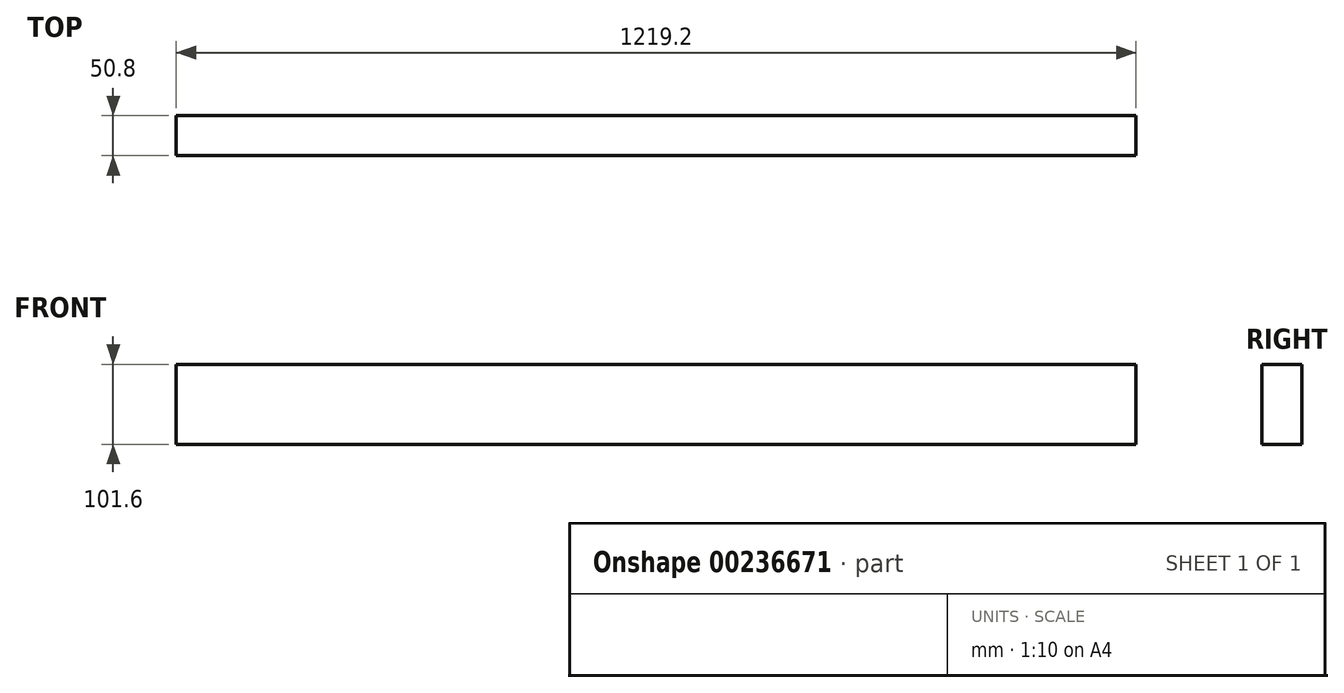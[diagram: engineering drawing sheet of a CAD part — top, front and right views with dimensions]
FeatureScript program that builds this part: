
annotation { "Feature Type Name" : "Feature", "Feature Type Description" : "" }
export const myFeature = defineFeature(function(context is Context, id is Id, definition is map)
    precondition{}
    {
        {
            var Q0;
            Q0=qCreatedBy(makeId("Top.planeOp"),FACE);
            var sketch = newSketch(context, id + "F0", { "sketchPlane" : qUnion([Q0])});
            skLineSegment(sketch, "E0.bottom", {"start": v(609.6, 25.4) * mm, "end": v(-609.6, 25.4) * mm});
            skLineSegment(sketch, "E0.top", {"start": v(609.6, -25.4) * mm, "end": v(-609.6, -25.4) * mm});
            skLineSegment(sketch, "E0.left", {"start": v(609.6, 25.4) * mm, "end": v(609.6, -25.4) * mm});
            skLineSegment(sketch, "E0.right", {"start": v(-609.6, 25.4) * mm, "end": v(-609.6, -25.4) * mm});
            skPoint(sketch, "E0.middle", {"position": v(0, 0) * mm});
            skSolve(sketch);
        }
        {
            var Q0;
            Q0 = qSketchRegion(id + "F0", true);
            extrude(context, id + "F1", {"entities" : qUnion([Q0]), "endBound" : BoundingType.SYMMETRIC, "depth" : 101.6 * mm});
        }
    });
